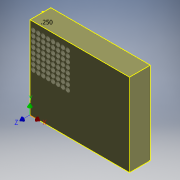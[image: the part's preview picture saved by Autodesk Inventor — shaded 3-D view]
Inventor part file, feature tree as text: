
AUTODESK INVENTOR PART (.ipt)
format: ipt  version: 2018 (Build 220112000, 112)  size: 11,441,664 bytes
history: native  units: mm (DEFAULTED — no unit token found)
features: other x256, loft x64, extrude x6, sketch x3, fillet x1
ambient origin geometry x8: Origin, YZ Plane, XZ Plane, XY Plane, X Axis, Y Axis, Z Axis, Center Point
bodies: Solid1 (feature_tree)
feature tree (330):
  extrude  "Extrusion1"  Depth=127.254mm
  sketch  "Sketch2"  dims[d2=32.004mm d3=0.0mm d4=5.2578mm]
  extrude  "Extrusion2"  Depth=5.2578mm
  extrude  "Extrusion3"  Depth=7.5692mm
  sketch  "Sketch3"  dims[d5=11.6713mm d6=7.5692mm d7=5.26mm d8=7.5692mm d9=5.2578mm d10=7.5692mm d11=7.5692mm d12=5.2578mm d13=7.5692mm d14=7.5692mm d15=7.5692mm d16=7.5692mm d17=7.5692mm d18=7.5692mm d19=7.5692mm d20=7.5692mm d21=7.5692mm d22=7.5692mm d23=3.6576mm d24=14.6558mm d25=0.0mm d26=3.6576mm d27=3.6576mm d28=3.6576mm d29=3.6576mm d30=3.6576mm d31=3.6576mm d32=3.6576mm d33=3.6576mm d34=3.6576mm d35=3.6576mm d36=3.6576mm d37=3.6576mm d38=3.6576mm d39=3.6576mm d40=3.6576mm d41=3.6576mm d42=3.6576mm d43=3.6576mm d44=3.6576mm d45=3.6576mm d46=3.6576mm d47=3.6576mm d48=3.6576mm d49=3.6576mm d50=3.6576mm d51=3.6576mm d52=3.6576mm d53=3.6576mm d54=3.6576mm d55=3.6576mm d56=3.6576mm d57=3.6576mm d58=3.6576mm d59=3.6576mm d60=3.6576mm d61=3.6576mm d62=3.6576mm d63=3.6576mm d64=3.6576mm d65=3.6576mm d66=3.6576mm d67=3.6576mm d68=3.6576mm d69=3.6576mm d70=3.6576mm d71=3.6576mm d72=3.6576mm d73=3.6576mm d74=3.6576mm d75=3.6576mm d76=3.6576mm d77=3.6576mm d78=3.6576mm d79=5.8166mm d80=3.6576mm d81=3.6576mm d82=3.6576mm d83=3.6576mm d84=3.6576mm d85=3.6576mm d86=3.6576mm d87=3.6576mm d88=3.6576mm d89=3.6576mm d90=19.812mm d91=0.0mm d92=6.35mm d93=5.8166mm d94=5.8166mm d95=5.8166mm d96=5.8166mm d97=5.8166mm d98=5.8166mm d99=5.8166mm d100=5.8166mm d101=5.8166mm d102=5.8166mm d103=5.8166mm d104=5.8166mm d105=5.8166mm d106=5.8166mm d107=5.8166mm d108=5.8166mm d109=5.8166mm d110=5.8166mm d111=5.8166mm d112=5.8166mm d113=5.8166mm d114=5.8166mm d115=5.8166mm d116=5.8166mm d117=5.8166mm d118=5.8166mm d119=5.8166mm d120=5.8166mm d121=5.8166mm d122=5.8166mm d123=5.8166mm d124=5.8166mm d125=5.8166mm d126=5.8166mm d127=5.8166mm d128=5.8166mm d129=5.8166mm d130=5.8166mm d131=5.8166mm d132=5.8166mm d133=5.8166mm d134=5.8166mm d135=5.8166mm d136=5.8166mm d137=5.8166mm d138=3.6576mm d139=5.8166mm d140=5.8166mm d141=5.8166mm d142=5.8166mm d143=5.8166mm d144=5.8166mm d145=5.8166mm d146=5.8166mm d147=5.8166mm d148=5.8166mm d149=5.8166mm d150=5.8166mm d151=5.8166mm d152=5.8166mm d153=5.8166mm d154=5.8166mm d155=5.8166mm d156=5.8166mm d159=9.398mm d160=0.0mm d161=6.2738mm d162=6.2738mm d163=6.2738mm d164=6.2738mm d165=6.2738mm d166=6.2738mm d167=6.2738mm d168=6.2738mm d169=6.2738mm d170=6.2738mm d171=6.2738mm d172=6.2738mm d173=6.2738mm d174=6.2738mm d175=6.2738mm d176=6.2738mm d177=6.2738mm d178=6.2738mm d179=6.2738mm d180=6.2738mm d181=6.2738mm d182=6.2738mm d183=6.2738mm d184=6.2738mm d185=6.2738mm d186=6.2738mm d187=6.2738mm d188=6.2738mm d189=6.2738mm d190=6.2738mm d191=6.2738mm d192=6.2738mm d193=6.2738mm d194=6.2738mm d195=6.2738mm d196=6.2738mm d197=6.2738mm d198=6.2738mm d199=6.2738mm d200=6.2738mm d201=6.2738mm d202=6.2738mm d203=6.2738mm d204=6.2738mm d205=6.2738mm d206=6.2738mm d207=6.2738mm d208=6.2738mm d209=6.2738mm d210=6.2738mm d211=6.2738mm d212=6.2738mm d213=6.2738mm d214=6.2738mm d215=6.2738mm d216=6.2738mm d217=6.2738mm d218=6.2738mm d219=6.2738mm d220=6.2738mm d221=6.2738mm d222=6.2738mm d223=6.2738mm d224=6.2738mm d225=9.398mm d226=0.0mm d227=6.9596mm d228=6.9596mm d229=6.9596mm d230=6.9596mm d231=6.9596mm d232=6.9596mm d233=6.9596mm d234=6.9596mm d235=6.9596mm d236=6.9596mm d237=6.9596mm d238=6.9596mm d239=6.9596mm d240=6.9596mm d241=6.9596mm d242=6.9596mm d243=6.9596mm d244=6.9596mm d245=6.9596mm d246=6.9596mm d247=6.9596mm d248=6.9596mm d249=6.9596mm d250=6.9596mm d251=6.9596mm d252=6.9596mm d253=6.9596mm d254=6.9596mm d255=6.9596mm d256=6.9596mm d257=6.9596mm d258=6.9596mm d259=6.9596mm d260=6.9596mm d261=6.9596mm d262=6.9596mm d263=6.9596mm d264=6.9596mm d265=6.9596mm d266=6.9596mm d267=6.9596mm d268=6.9596mm d269=6.9596mm d270=6.9596mm d271=6.9596mm d272=6.9596mm d273=6.9596mm d274=6.9596mm d275=6.9596mm d276=6.9596mm d277=6.9596mm d278=6.9596mm d279=6.9596mm d280=6.9596mm d281=6.9596mm d282=6.9596mm d283=6.9596mm d284=6.9596mm d285=6.9596mm d286=6.9596mm d287=6.9596mm d288=6.9596mm d289=6.9596mm d290=6.9596mm d291=4.1148mm d292=0.0mm d293=1.8288mm d294=0.0mm d295=90.0deg d296=0.0mm d297=90.0deg d298=0.0mm d299=90.0deg d300=0.0mm d301=90.0deg d302=0.0mm d303=90.0deg d304=0.0mm d305=90.0deg d306=0.0mm d307=90.0deg d308=0.0mm d309=90.0deg d310=0.0mm d311=90.0deg d312=0.0mm d313=90.0deg d314=0.0mm d315=90.0deg d316=0.0mm d317=90.0deg d318=0.0mm d319=90.0deg d320=0.0mm d321=90.0deg d322=0.0mm d323=90.0deg d324=0.0mm d325=90.0deg d326=0.0mm d327=90.0deg d328=0.0mm d329=90.0deg d330=0.0mm d331=90.0deg d332=0.0mm d333=90.0deg d334=0.0mm d335=90.0deg d336=0.0mm d337=90.0deg d338=0.0mm d339=90.0deg d340=0.0mm d341=90.0deg d342=0.0mm d343=90.0deg d344=0.0mm d345=90.0deg d346=0.0mm d347=90.0deg d348=0.0mm d349=90.0deg d350=0.0mm d351=90.0deg d352=0.0mm d353=90.0deg d354=0.0mm d355=90.0deg d356=0.0mm d357=90.0deg d358=0.0mm d359=90.0deg d360=0.0mm d361=90.0deg d362=0.0mm d363=90.0deg d364=0.0mm d365=90.0deg d366=0.0mm d367=90.0deg d368=0.0mm d369=90.0deg d370=0.0mm d371=90.0deg d372=0.0mm d373=90.0deg d374=0.0mm d375=90.0deg d376=0.0mm d377=90.0deg d378=0.0mm d379=90.0deg d380=0.0mm d381=90.0deg d382=0.0mm d383=90.0deg d384=0.0mm d385=90.0deg d386=0.0mm d387=90.0deg d388=0.0mm d389=90.0deg d390=0.0mm d391=90.0deg d392=0.0mm d393=90.0deg d394=0.0mm d395=90.0deg d396=0.0mm d397=90.0deg d398=0.0mm d399=90.0deg d400=0.0mm d401=90.0deg d402=0.0mm d403=90.0deg d404=0.0mm d405=90.0deg d406=0.0mm d407=90.0deg d408=0.0mm d409=90.0deg d410=0.0mm d411=90.0deg d412=0.0mm d413=90.0deg d414=0.0mm d415=90.0deg d416=0.0mm d417=90.0deg d418=0.0mm d419=90.0deg d420=0.0mm d421=90.0deg d422=0.0mm d423=90.0deg d424=0.0mm d425=90.0deg d426=0.0mm d427=90.0deg d428=0.0mm d429=90.0deg d430=0.0mm d431=90.0deg d432=0.0mm d433=90.0deg d434=0.0mm d435=90.0deg d436=0.0mm d437=90.0deg d438=0.0mm d439=90.0deg d440=0.0mm d441=90.0deg d442=0.0mm d443=90.0deg d444=0.0mm d445=90.0deg d446=0.0mm d447=90.0deg d448=0.0mm d449=90.0deg d450=0.0mm d451=90.0deg d452=0.0mm d453=90.0deg d454=0.0mm d455=90.0deg d456=0.0mm d457=90.0deg d458=0.0mm d459=90.0deg d460=0.0mm d461=90.0deg d462=0.0mm d463=90.0deg d464=0.0mm d465=90.0deg d466=0.0mm d467=90.0deg d468=0.0mm d469=90.0deg d470=0.0mm d471=90.0deg d472=0.0mm d473=90.0deg d474=0.0mm d475=90.0deg d476=0.0mm d477=90.0deg d478=0.0mm d479=90.0deg d480=0.0mm d481=90.0deg d482=0.0mm d483=90.0deg d484=0.0mm d485=90.0deg d486=0.0mm d487=90.0deg d488=0.0mm d489=90.0deg d490=0.0mm d491=90.0deg d492=0.0mm d493=90.0deg d494=0.0mm d495=90.0deg d496=0.0mm d497=90.0deg d498=0.0mm d499=90.0deg d500=0.0mm d501=90.0deg d502=0.0mm d503=90.0deg d504=0.0mm d505=90.0deg d506=0.0mm d507=90.0deg d508=0.0mm d509=90.0deg d510=0.0mm d511=90.0deg d512=0.0mm d513=90.0deg d514=0.0mm d515=90.0deg d516=0.0mm d517=90.0deg d518=0.0mm d519=90.0deg d520=0.0mm d521=90.0deg d522=0.0mm d523=90.0deg d524=0.0mm d525=90.0deg d526=0.0mm d527=90.0deg d528=0.0mm d529=90.0deg d530=0.0mm d531=90.0deg d532=0.0mm d533=90.0deg d534=0.0mm d535=90.0deg d536=0.0mm d537=90.0deg d538=0.0mm d539=90.0deg d540=0.0mm d541=90.0deg d542=0.0mm d543=90.0deg d544=0.0mm d545=90.0deg d546=0.0mm d547=90.0deg d548=0.0mm d549=90.0deg d550=0.0mm d551=90.0deg d552=0.0mm d553=90.0deg d554=0.0mm d555=90.0deg d556=0.0mm d557=90.0deg d558=0.0mm d559=90.0deg d560=0.0mm d561=90.0deg d562=0.0mm d563=90.0deg d564=0.0mm d565=90.0deg d566=0.0mm d567=90.0deg d568=0.0mm d569=90.0deg d570=0.0mm d571=90.0deg d572=0.0mm d573=90.0deg d574=0.0mm d575=90.0deg d576=0.0mm d577=90.0deg d578=0.0mm d579=90.0deg d580=0.0mm d581=90.0deg d582=0.0mm d583=90.0deg d584=0.0mm d585=90.0deg d586=0.0mm d587=90.0deg d588=0.0mm d589=90.0deg d590=0.0mm d591=90.0deg d592=0.0mm d593=90.0deg d594=0.0mm d595=90.0deg d596=0.0mm d597=90.0deg d598=0.0mm d599=90.0deg d600=0.0mm d601=90.0deg d602=0.0mm d603=90.0deg d604=0.0mm d605=90.0deg d606=0.0mm d607=90.0deg d608=0.0mm d609=90.0deg d610=0.0mm d611=90.0deg d612=0.0mm d613=90.0deg d614=0.0mm d615=90.0deg d616=0.0mm d617=90.0deg d618=0.0mm d619=90.0deg d620=0.0mm d621=90.0deg d622=0.0mm d623=90.0deg d624=0.0mm d625=90.0deg d626=0.0mm d627=90.0deg d628=0.0mm d629=90.0deg d630=0.0mm d631=90.0deg d632=0.0mm d633=90.0deg d634=0.0mm d635=90.0deg d636=0.0mm d637=90.0deg d638=0.0mm d639=90.0deg d640=0.0mm d641=90.0deg d642=0.0mm d643=90.0deg d644=0.0mm d645=90.0deg d646=0.0mm d647=90.0deg d648=0.0mm d649=90.0deg d650=0.0mm d651=90.0deg d652=0.0mm d653=90.0deg d654=0.0mm d655=90.0deg d656=0.0mm d657=90.0deg d658=0.0mm d659=90.0deg d660=0.0mm d661=90.0deg d662=0.0mm d663=90.0deg d664=0.0mm d665=90.0deg d666=0.0mm d667=90.0deg d668=0.0mm d669=90.0deg d670=0.0mm d671=90.0deg d672=0.0mm d673=90.0deg d674=0.0mm d675=90.0deg d676=0.0mm d677=90.0deg d678=0.0mm d679=90.0deg d680=0.0mm d681=90.0deg d682=0.0mm d683=90.0deg d684=0.0mm d685=90.0deg d686=0.0mm d687=90.0deg d688=0.0mm d689=90.0deg d690=0.0mm d691=90.0deg d692=0.0mm d693=90.0deg d694=0.0mm d695=90.0deg d696=0.0mm d697=90.0deg d698=0.0mm d699=90.0deg d700=0.0mm d701=90.0deg d702=0.0mm d703=90.0deg d704=0.0mm d705=90.0deg d706=0.0mm d707=90.0deg d708=0.0mm d709=90.0deg d710=0.0mm d711=90.0deg d712=0.0mm d713=90.0deg d714=0.0mm d715=90.0deg d716=0.0mm d717=90.0deg d718=0.0mm d719=90.0deg d720=0.0mm d721=90.0deg d722=0.0mm d723=90.0deg d724=0.0mm d725=90.0deg d726=0.0mm d727=90.0deg d728=0.0mm d729=90.0deg d730=0.0mm d731=90.0deg d732=0.0mm d733=90.0deg d734=0.0mm d735=90.0deg d736=0.0mm d737=90.0deg d738=0.0mm d739=90.0deg d740=0.0mm d741=90.0deg d742=0.0mm d743=90.0deg d744=0.0mm d745=90.0deg d746=0.0mm d747=90.0deg d748=0.0mm d749=90.0deg d750=0.0mm d751=90.0deg d752=0.0mm d753=90.0deg d754=0.0mm d755=90.0deg d756=0.0mm d757=90.0deg d758=0.0mm d759=90.0deg d760=0.0mm d761=90.0deg d762=0.0mm d763=90.0deg d764=0.0mm d765=90.0deg d766=0.0mm d767=90.0deg d768=0.0mm d769=90.0deg d770=0.0mm d771=90.0deg d772=0.0mm d773=90.0deg d774=0.0mm d775=90.0deg d776=0.0mm d777=90.0deg d778=0.0mm d779=90.0deg d780=0.0mm d781=90.0deg d782=0.0mm d783=90.0deg d784=0.0mm d785=90.0deg d786=0.0mm d787=90.0deg d788=0.0mm d789=90.0deg d790=0.0mm d791=90.0deg d792=0.0mm d793=90.0deg d794=0.0mm d795=90.0deg d796=0.0mm d797=90.0deg d798=0.0mm d799=90.0deg d800=0.0mm d801=90.0deg d802=0.0mm d803=90.0deg d804=0.0mm d805=90.0deg]
  extrude  "Extrusion4"  Depth=5.26mm
  extrude  "Extrusion5"  Depth=7.5692mm
  extrude  "Extrusion6"  Depth=5.2578mm
  fillet  "Fillet1"  Radius=7.5692mm
  loft  "Loft1"
  loft  "Loft2"
  loft  "Loft3"
  loft  "Loft4"
  loft  "Loft5"
  loft  "Loft6"
  loft  "Loft7"
  loft  "Loft8"
  loft  "Loft9"
  loft  "Loft10"
  loft  "Loft11"
  loft  "Loft12"
  loft  "Loft13"
  loft  "Loft14"
  loft  "Loft15"
  loft  "Loft16"
  loft  "Loft17"
  loft  "Loft18"
  loft  "Loft19"
  loft  "Loft20"
  loft  "Loft21"
  loft  "Loft22"
  loft  "Loft23"
  loft  "Loft24"
  loft  "Loft25"
  loft  "Loft26"
  loft  "Loft27"
  loft  "Loft28"
  loft  "Loft29"
  loft  "Loft30"
  loft  "Loft31"
  loft  "Loft32"
  loft  "Loft33"
  loft  "Loft34"
  loft  "Loft35"
  loft  "Loft36"
  loft  "Loft37"
  loft  "Loft38"
  loft  "Loft39"
  loft  "Loft40"
  loft  "Loft41"
  loft  "Loft42"
  loft  "Loft43"
  loft  "Loft44"
  loft  "Loft45"
  loft  "Loft46"
  loft  "Loft47"
  loft  "Loft48"
  loft  "Loft49"
  loft  "Loft50"
  loft  "Loft51"
  loft  "Loft52"
  loft  "Loft53"
  loft  "Loft54"
  loft  "Loft55"
  loft  "Loft56"
  loft  "Loft57"
  loft  "Loft58"
  loft  "Loft59"
  loft  "Loft60"
  loft  "Loft61"
  loft  "Loft62"
  loft  "Loft63"
  loft  "Loft64"
  sketch  "Sketch1"  dims[d0=153.162mm d1=127.254mm]
  other  "Edges1"
  other  "Edges2"
  other  "Edges3"
  other  "Edges4"
  other  "Edges5"
  other  "Edges6"
  other  "Edges7"
  other  "Edges8"
  other  "Edges9"
  other  "Edges10"
  other  "Edges11"
  other  "Edges12"
  other  "Edges13"
  other  "Edges14"
  other  "Edges15"
  other  "Edges16"
  other  "Edges17"
  other  "Edges18"
  other  "Edges19"
  other  "Edges20"
  other  "Edges21"
  other  "Edges22"
  other  "Edges23"
  other  "Edges24"
  other  "Edges25"
  other  "Edges26"
  other  "Edges27"
  other  "Edges28"
  other  "Edges29"
  other  "Edges30"
  other  "Edges31"
  other  "Edges32"
  other  "Edges33"
  other  "Edges34"
  other  "Edges35"
  other  "Edges36"
  other  "Edges37"
  other  "Edges38"
  other  "Edges39"
  other  "Edges40"
  other  "Edges41"
  other  "Edges42"
  other  "Edges43"
  other  "Edges44"
  other  "Edges45"
  other  "Edges46"
  other  "Edges47"
  other  "Edges48"
  other  "Edges49"
  other  "Edges50"
  other  "Edges51"
  other  "Edges52"
  other  "Edges53"
  other  "Edges54"
  other  "Edges55"
  other  "Edges56"
  other  "Edges57"
  other  "Edges58"
  other  "Edges59"
  other  "Edges60"
  other  "Edges61"
  other  "Edges62"
  other  "Edges63"
  other  "Edges64"
  other  "Edges65"
  other  "Edges66"
  other  "Edges67"
  other  "Edges68"
  other  "Edges69"
  other  "Edges70"
  other  "Edges71"
  other  "Edges72"
  other  "Edges73"
  other  "Edges74"
  other  "Edges75"
  other  "Edges76"
  other  "Edges77"
  other  "Edges78"
  other  "Edges79"
  other  "Edges80"
  other  "Edges81"
  other  "Edges82"
  other  "Edges83"
  other  "Edges84"
  other  "Edges85"
  other  "Edges86"
  other  "Edges87"
  other  "Edges88"
  other  "Edges89"
  other  "Edges90"
  other  "Edges91"
  other  "Edges92"
  other  "Edges93"
  other  "Edges94"
  other  "Edges95"
  other  "Edges96"
  other  "Edges97"
  other  "Edges98"
  other  "Edges99"
  other  "Edges100"
  other  "Edges101"
  other  "Edges102"
  other  "Edges103"
  other  "Edges104"
  other  "Edges105"
  other  "Edges106"
  other  "Edges107"
  other  "Edges108"
  other  "Edges109"
  other  "Edges110"
  other  "Edges111"
  other  "Edges112"
  other  "Edges113"
  other  "Edges114"
  other  "Edges115"
  other  "Edges116"
  other  "Edges117"
  other  "Edges118"
  other  "Edges119"
  other  "Edges120"
  other  "Edges121"
  other  "Edges122"
  other  "Edges123"
  other  "Edges124"
  other  "Edges125"
  other  "Edges126"
  other  "Edges127"
  other  "Edges128"
  other  "Edges129"
  other  "Edges130"
  other  "Edges131"
  other  "Edges132"
  other  "Edges133"
  other  "Edges134"
  other  "Edges135"
  other  "Edges136"
  other  "Edges137"
  other  "Edges138"
  other  "Edges139"
  other  "Edges140"
  other  "Edges141"
  other  "Edges142"
  other  "Edges143"
  other  "Edges144"
  other  "Edges145"
  other  "Edges146"
  other  "Edges147"
  other  "Edges148"
  other  "Edges149"
  other  "Edges150"
  other  "Edges151"
  other  "Edges152"
  other  "Edges153"
  other  "Edges154"
  other  "Edges155"
  other  "Edges156"
  other  "Edges157"
  other  "Edges158"
  other  "Edges159"
  other  "Edges160"
  other  "Edges161"
  other  "Edges162"
  other  "Edges163"
  other  "Edges164"
  other  "Edges165"
  other  "Edges166"
  other  "Edges167"
  other  "Edges168"
  other  "Edges169"
  other  "Edges170"
  other  "Edges171"
  other  "Edges172"
  other  "Edges173"
  other  "Edges174"
  other  "Edges175"
  other  "Edges176"
  other  "Edges177"
  other  "Edges178"
  other  "Edges179"
  other  "Edges180"
  other  "Edges181"
  other  "Edges182"
  other  "Edges183"
  other  "Edges184"
  other  "Edges185"
  other  "Edges186"
  other  "Edges187"
  other  "Edges188"
  other  "Edges189"
  other  "Edges190"
  other  "Edges191"
  other  "Edges192"
  other  "Edges193"
  other  "Edges194"
  other  "Edges195"
  other  "Edges196"
  other  "Edges197"
  other  "Edges198"
  other  "Edges199"
  other  "Edges200"
  other  "Edges201"
  other  "Edges202"
  other  "Edges203"
  other  "Edges204"
  other  "Edges205"
  other  "Edges206"
  other  "Edges207"
  other  "Edges208"
  other  "Edges209"
  other  "Edges210"
  other  "Edges211"
  other  "Edges212"
  other  "Edges213"
  other  "Edges214"
  other  "Edges215"
  other  "Edges216"
  other  "Edges217"
  other  "Edges218"
  other  "Edges219"
  other  "Edges220"
  other  "Edges221"
  other  "Edges222"
  other  "Edges223"
  other  "Edges224"
  other  "Edges225"
  other  "Edges226"
  other  "Edges227"
  other  "Edges228"
  other  "Edges229"
  other  "Edges230"
  other  "Edges231"
  other  "Edges232"
  other  "Edges233"
  other  "Edges234"
  other  "Edges235"
  other  "Edges236"
  other  "Edges237"
  other  "Edges238"
  other  "Edges239"
  other  "Edges240"
  other  "Edges241"
  other  "Edges242"
  other  "Edges243"
  other  "Edges244"
  other  "Edges245"
  other  "Edges246"
  other  "Edges247"
  other  "Edges248"
  other  "Edges249"
  other  "Edges250"
  other  "Edges251"
  other  "Edges252"
  other  "Edges253"
  other  "Edges254"
  other  "Edges255"
  other  "Edges256"
